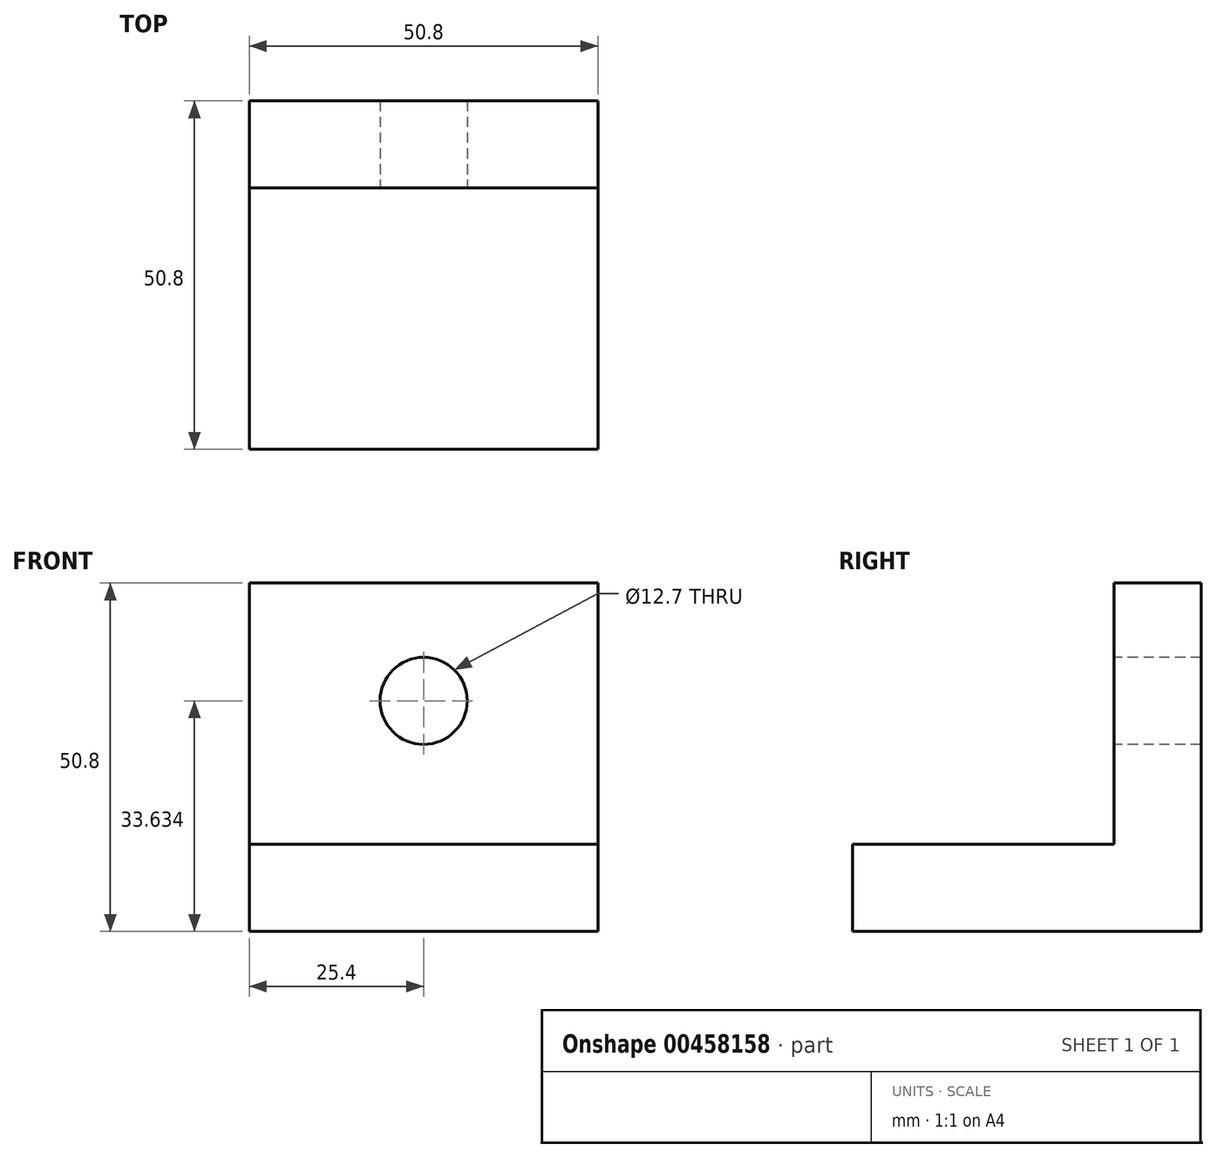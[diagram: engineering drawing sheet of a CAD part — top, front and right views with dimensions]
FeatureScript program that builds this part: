
annotation { "Feature Type Name" : "Feature", "Feature Type Description" : "" }
export const myFeature = defineFeature(function(context is Context, id is Id, definition is map)
    precondition{}
    {
        {
            var Q0;
            Q0=qCreatedBy(makeId("Front.planeOp"),FACE);
            var sketch = newSketch(context, id + "F0", { "sketchPlane" : qUnion([Q0])});
            skLineSegment(sketch, "E0", {"start": v(0, 0) * mm, "end": v(-50.8, 0) * mm});
            skLineSegment(sketch, "E1", {"start": v(-50.8, 50.8) * mm, "end": v(0, 50.8) * mm});
            skLineSegment(sketch, "E2", {"start": v(0, 0) * mm, "end": v(0, 50.8) * mm});
            skLineSegment(sketch, "E3", {"start": v(-50.8, 0) * mm, "end": v(-50.8, 50.8) * mm});
            skSolve(sketch);
        }
        {
            var Q0;
            Q0=qCreatedBy(makeId("Front.planeOp"),FACE);
            var sketch = newSketch(context, id + "F1", { "sketchPlane" : qUnion([Q0])});
            skLineSegment(sketch, "E4", {"start": v(0, 0) * mm, "end": v(0, 12.7) * mm});
            skLineSegment(sketch, "E5", {"start": v(0, 12.7) * mm, "end": v(-50.8, 12.7) * mm});
            skLineSegment(sketch, "E6", {"start": v(-50.8, 12.7) * mm, "end": v(-50.8, 0) * mm});
            skLineSegment(sketch, "E7", {"start": v(-50.8, 0) * mm, "end": v(0, 0) * mm});
            skSolve(sketch);
        }
        {
            var Q0;
            Q0=makeQuery(id+"F0.imprint","IMPRINT",FACE,{"disambiguationData":[TD([[makeQuery(id+"F0.imprint","IMPRINT",EDGE,{"derivedFrom":sQuery(id+"F0.wireOp",EDGE,"E0")}),-1.0]])]});
            extrude(context, id + "F2", {"entities" : qUnion([Q0]), "depth" : 12.7 * mm});
        }
        {
            var Q0;
            Q0 = qSketchRegion(id + "F1", true);
            extrude(context, id + "F3", {"entities" : qUnion([Q0]), "operationType" : NewBodyOperationType.ADD, "depth" : 50.8 * mm});
        }
        {
            var Q0;
            Q0=qCreatedBy(makeId("Front.planeOp"),FACE);
            var sketch = newSketch(context, id + "F4", { "sketchPlane" : qUnion([Q0])});
            skCircle(sketch, "E8", {"center": v(-25.4, 33.63) * mm, "radius": 6.35 * mm});
            skSolve(sketch);
        }
        {
            var Q0;
            Q0=makeQuery(id+"F4.imprint","IMPRINT",FACE,{"disambiguationData":[TD([[makeQuery(id+"F4.imprint","IMPRINT",EDGE,{"derivedFrom":sQuery(id+"F4.wireOp",EDGE,"E8")}),1.0]])]});
            extrude(context, id + "F5", {"entities" : qUnion([Q0]), "operationType" : NewBodyOperationType.REMOVE, "endBound" : BoundingType.SYMMETRIC, "oppositeDirection" : true, "depth" : 62.48 * mm});
        }
    });
